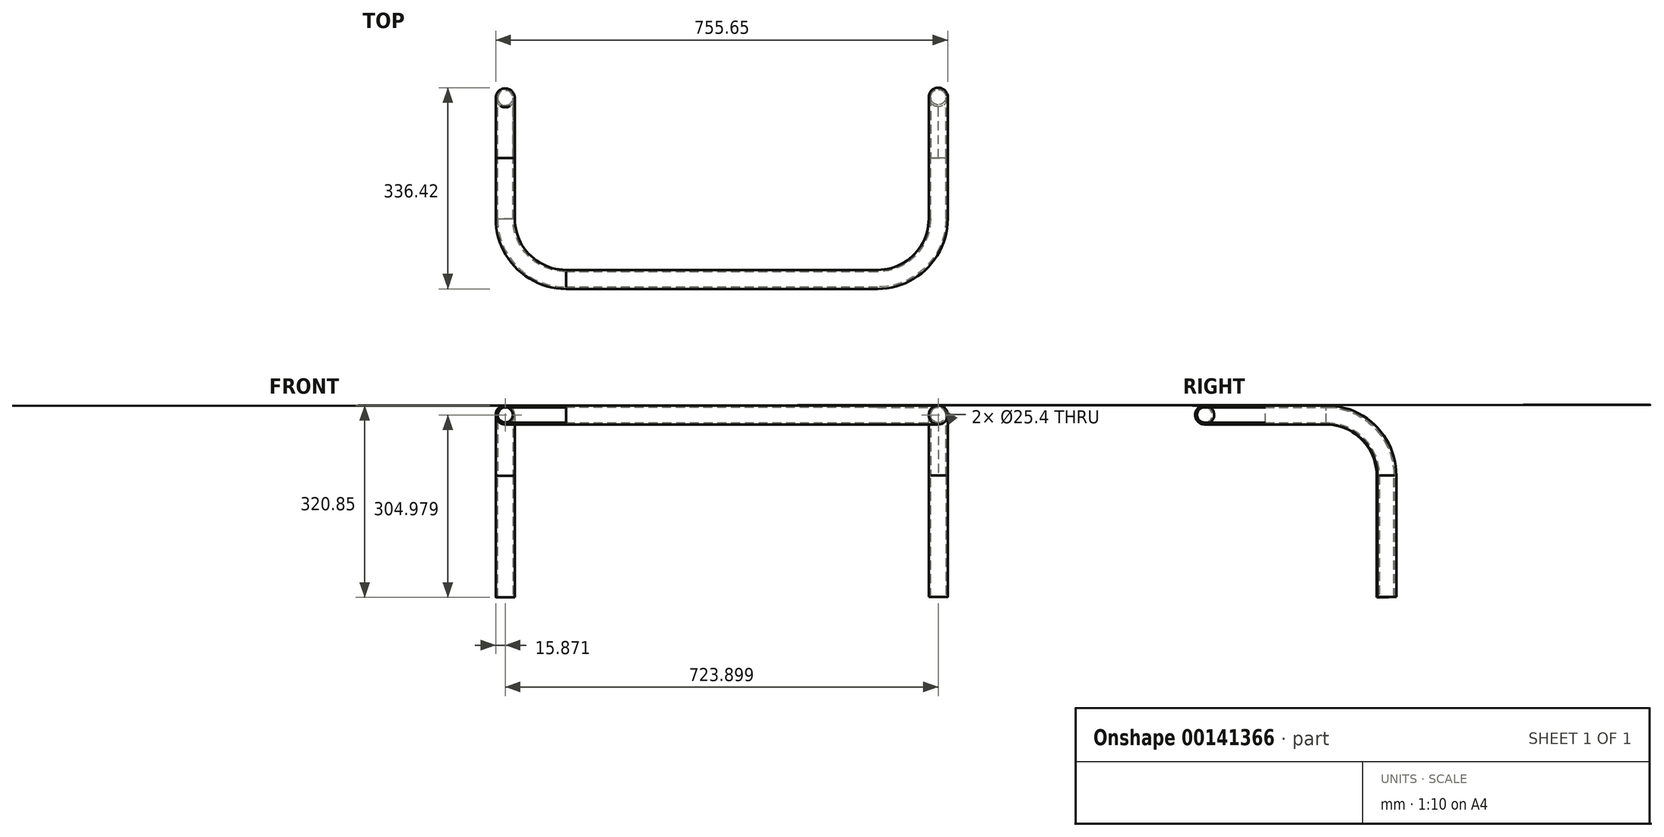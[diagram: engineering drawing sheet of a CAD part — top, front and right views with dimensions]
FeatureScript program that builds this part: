
annotation { "Feature Type Name" : "Feature", "Feature Type Description" : "" }
export const myFeature = defineFeature(function(context is Context, id is Id, definition is map)
    precondition{}
    {
        {
            var Q0;
            Q0=qCreatedBy(makeId("Front.planeOp"),FACE);
            var sketch = newSketch(context, id + "F0", { "sketchPlane" : qUnion([Q0])});
            skLineSegment(sketch, "E0", {"start": v(-57.71, 3.81) * mm, "end": v(-57.71, 207.01) * mm});
            skLineSegment(sketch, "E1", {"start": v(666.19, 207.01) * mm, "end": v(666.19, 3.81) * mm});
            skLineSegment(sketch, "E2", {"start": v(43.89, 308.61) * mm, "end": v(564.59, 308.61) * mm});
            skSolve(sketch);
        }
        {
            var Q0;
            Q0=sQuery(id+"F0.wireOp",EDGE,"mjDuWlF3-Q2C5-AVhh-5H8Y-v2cNqstjDBgE");
            var Q1;
            Q1=sQuery(id+"F0.wireOp",EDGE,"E2");
            cPlane(context, id + "F1", {"entities" : qUnion([Q0, Q1]), "cplaneType" : CPlaneType.LINE_ANGLE, "offset" : 25.4 * mm, "angle" : 90 * degree, "width" : 152.4 * mm, "height" : 152.4 * mm});
        }
        {
            var Q0;
            Q0=qCreatedBy(id+"F1.planeOp",FACE);
            var sketch = newSketch(context, id + "F2", { "sketchPlane" : qUnion([Q0])});
            skLineSegment(sketch, "E3", {"start": v(665.66, -202.81) * mm, "end": v(665.66, -304.41) * mm});
            skLineSegment(sketch, "E4", {"start": v(-58.24, -304.41) * mm, "end": v(-58.24, -202.81) * mm});
            skLineSegment(sketch, "E5", {"start": v(348.15, -304.41) * mm, "end": v(348.15, -202.81) * mm});
            skSolve(sketch);
        }
        {
            var Q0;
            Q0=qCreatedBy(makeId("Top.planeOp"),FACE);
            var sketch = newSketch(context, id + "F3", { "sketchPlane" : qUnion([Q0])});
            skLineSegment(sketch, "E6", {"start": v(-58.24, -304.41) * mm, "end": v(-58.24, -101.21) * mm});
            skCircle(sketch, "E7", {"center": v(-57.71, 0) * mm, "radius": 15.88 * mm});
            skSolve(sketch);
        }
        {
            var Q0;
            Q0=sQuery(id+"F2.wireOp",VERTEX,"E4.start");
            var Q1;
            Q1=sQuery(id+"F2.wireOp",VERTEX,"E5.start");
            var Q2;
            Q2=sQuery(id+"F3.wireOp",VERTEX,"E6.start");
            cPlane(context, id + "F4", {"entities" : qUnion([Q0, Q1, Q2]), "cplaneType" : CPlaneType.THREE_POINT, "offset" : 25.4 * mm, "width" : 152.4 * mm, "height" : 152.4 * mm});
        }
        {
            var Q0;
            Q0=qCreatedBy(id+"F4.planeOp",FACE);
            var sketch = newSketch(context, id + "F5", { "sketchPlane" : qUnion([Q0])});
            skCircle(sketch, "E8", {"center": v(-58.24, 324.49) * mm, "radius": 15.88 * mm});
            skCircle(sketch, "E9.1.0.0", {"center": v(665.66, 324.49) * mm, "radius": 15.88 * mm});
            skLineSegment(sketch, "E9.direction1", {"start": v(-58.24, 324.49) * mm, "end": v(665.66, 324.49) * mm, "construction": true});
            skSolve(sketch);
        }
        {
            var Q0;
            Q0=makeQuery(id+"F5.imprint","IMPRINT",FACE,{"disambiguationData":[TD([[makeQuery(id+"F5.imprint","IMPRINT",EDGE,{"derivedFrom":sQuery(id+"F5.wireOp",EDGE,"E8")}),1.0]])]});
            var Q1;
            Q1=sQuery(id+"F2.wireOp",EDGE,"E4");
            sweep(context, id + "F6", {"profiles" : qUnion([Q0]), "path" : qUnion([Q1])});
        }
        {
            var Q0;
            Q0=qCreatedBy(makeId("Right.planeOp"),FACE);
            var sketch = newSketch(context, id + "F7", { "sketchPlane" : qUnion([Q0])});
            skArc(sketch, "E10", {"start": v(2.2, 217.22) * mm, "mid": v(-27.59, 288.26) * mm, "end": v(-98.67, 317.97) * mm});
            skSolve(sketch);
        }
        {
            var Q0;
            Q0=makeQuery(id+"F6.opSweep","CAP_FACE",FACE,{"disambiguationData":[OSD([sQuery(id+"F2.wireOp",VERTEX,"E4.end"),sQuery(id+"F5.wireOp",EDGE,"E8")])],"isStart":false});
            var sketch = newSketch(context, id + "F8", { "sketchPlane" : qUnion([Q0])});
            skLineSegment(sketch, "E11", {"start": v(58.24, 324.49) * mm, "end": v(-68.76, 324.49) * mm});
            skSolve(sketch);
        }
        {
            var Q0;
            Q0 = qBodyType(qCreatedBy(id + "F8" ,EDGE), BodyType.WIRE);
            cPlane(context, id + "F9", {"entities" : qUnion([Q0]), "cplaneType" : CPlaneType.LINE_ANGLE, "offset" : 25.4 * mm, "angle" : 90 * degree, "width" : 152.4 * mm, "height" : 152.4 * mm});
        }
        {
            var Q0;
            Q0=qCreatedBy(id+"F9.planeOp",FACE);
            var sketch = newSketch(context, id + "F10", { "sketchPlane" : qUnion([Q0])});
            skLineSegment(sketch, "E12", {"start": v(-58.27, -202.8) * mm, "end": v(-58.27, -75.8) * mm});
            skSolve(sketch);
        }
        {
            var Q0;
            Q0=sQuery(id+"F10.wireOp",EDGE,"E12");
            cPlane(context, id + "F11", {"entities" : qUnion([Q0]), "cplaneType" : CPlaneType.LINE_ANGLE, "offset" : 25.4 * mm, "angle" : 90 * degree, "width" : 152.4 * mm, "height" : 152.4 * mm});
        }
        {
            var Q0;
            Q0=qCreatedBy(id+"F11.planeOp",FACE);
            var sketch = newSketch(context, id + "F12", { "sketchPlane" : qUnion([Q0])});
            skLineSegment(sketch, "E13", {"start": v(-102.45, 324.5) * mm, "end": v(-204.05, 324.5) * mm});
            skLineSegment(sketch, "E14", {"start": v(-204.05, 324.5) * mm, "end": v(-204.05, 222.9) * mm});
            skArc(sketch, "E15", {"start": v(-102.45, 222.9) * mm, "mid": v(-132.21, 294.75) * mm, "end": v(-204.05, 324.5) * mm});
            skLineSegment(sketch, "E16", {"start": v(-204.05, 222.9) * mm, "end": v(-102.45, 222.9) * mm});
            skSolve(sketch);
        }
        {
            var Q0;
            Q0=makeQuery(id+"F6.opSweep","CAP_FACE",FACE,{"disambiguationData":[OSD([sQuery(id+"F2.wireOp",VERTEX,"E4.end"),sQuery(id+"F5.wireOp",EDGE,"E8")])],"isStart":false});
            var Q1;
            Q1=makeQuery(id+"F6.opSweep","CAP_FACE",FACE,{"disambiguationData":[OSD([sQuery(id+"F2.wireOp",VERTEX,"E4.end"),sQuery(id+"F5.wireOp",EDGE,"E9.1.0.0")])],"isStart":false});
            var Q2;
            Q2=sQuery(id+"F12.wireOp",EDGE,"E15");
            sweep(context, id + "F13", {"operationType" : NewBodyOperationType.ADD, "profiles" : qUnion([Q0, Q1]), "path" : qUnion([Q2])});
        }
        {
            var Q0;
            Q0=makeQuery(id+"F13.opSweep","CAP_FACE",FACE,{"disambiguationData":[OSD([sQuery(id+"F2.wireOp",VERTEX,"E4.end"),sQuery(id+"F5.wireOp",EDGE,"E8"),sQuery(id+"F7.wireOp",VERTEX,"E10.start")])],"isStart":false});
            var Q1;
            Q1=makeQuery(id+"F13.opSweep","CAP_FACE",FACE,{"disambiguationData":[OSD([sQuery(id+"F2.wireOp",VERTEX,"E4.end"),sQuery(id+"F5.wireOp",EDGE,"E9.1.0.0"),sQuery(id+"F7.wireOp",VERTEX,"E10.start")])],"isStart":false});
            var Q2;
            Q2=sQuery(id+"F0.wireOp",EDGE,"E0");
            sweep(context, id + "F14", {"operationType" : NewBodyOperationType.ADD, "profiles" : qUnion([Q0, Q1]), "path" : qUnion([Q2])});
        }
        {
            var Q0;
            Q0=makeQuery(id+"F6.opSweep","CAP_FACE",FACE,{"disambiguationData":[OSD([sQuery(id+"F2.wireOp",VERTEX,"E4.start"),sQuery(id+"F5.wireOp",EDGE,"E8")])],"isStart":true});
            var sketch = newSketch(context, id + "F15", { "sketchPlane" : qUnion([Q0])});
            skLineSegment(sketch, "E17", {"start": v(-58.24, 324.49) * mm, "end": v(-397.35, 324.49) * mm});
            skSolve(sketch);
        }
        {
            var Q0;
            Q0=sQuery(id+"F15.wireOp",EDGE,"E17");
            cPlane(context, id + "F16", {"entities" : qUnion([Q0]), "cplaneType" : CPlaneType.LINE_ANGLE, "offset" : 25.4 * mm, "angle" : 90 * degree, "width" : 152.4 * mm, "height" : 152.4 * mm});
        }
        {
            var Q0;
            Q0=qCreatedBy(id+"F16.planeOp",FACE);
            var sketch = newSketch(context, id + "F17", { "sketchPlane" : qUnion([Q0])});
            skLineSegment(sketch, "E18", {"start": v(-58.24, -304.42) * mm, "end": v(43.36, -304.42) * mm});
            skLineSegment(sketch, "E19", {"start": v(43.36, -304.42) * mm, "end": v(43.36, -406.02) * mm});
            skArc(sketch, "E20", {"start": v(-58.24, -304.42) * mm, "mid": v(-28.48, -376.26) * mm, "end": v(43.36, -406.02) * mm});
            skLineSegment(sketch, "E21", {"start": v(43.36, -304.42) * mm, "end": v(564.06, -304.42) * mm});
            skLineSegment(sketch, "E22", {"start": v(564.06, -304.42) * mm, "end": v(564.06, -406.02) * mm});
            skLineSegment(sketch, "E23", {"start": v(564.06, -304.42) * mm, "end": v(665.66, -304.42) * mm});
            skArc(sketch, "E24", {"start": v(564.06, -406.02) * mm, "mid": v(635.9, -376.26) * mm, "end": v(665.66, -304.42) * mm});
            skSolve(sketch);
        }
        {
            var Q0;
            Q0=makeQuery(id+"F15.imprint","IMPRINT",FACE,{"disambiguationData":[TD([[makeQuery(id+"F15.imprint","IMPRINT",EDGE,{"derivedFrom":makeQuery(id+"F6.opSweep","CAP_EDGE",EDGE,{"disambiguationData":[OSD([sQuery(id+"F2.wireOp",VERTEX,"E4.start"),sQuery(id+"F5.wireOp",EDGE,"E8")])],"isStart":true})}),-1.0]])]});
            var Q1;
            Q1=sQuery(id+"F17.wireOp",EDGE,"E20");
            sweep(context, id + "F18", {"operationType" : NewBodyOperationType.ADD, "profiles" : qUnion([Q0]), "path" : qUnion([Q1])});
        }
        {
            var Q0;
            Q0=makeQuery(id+"F18.opSweep","CAP_FACE",FACE,{"disambiguationData":[OSD([sQuery(id+"F2.wireOp",VERTEX,"E4.start"),sQuery(id+"F5.wireOp",EDGE,"E8"),sQuery(id+"F17.wireOp",VERTEX,"E20.end")])],"isStart":false});
            var Q1;
            Q1=sQuery(id+"F0.wireOp",EDGE,"E2");
            sweep(context, id + "F19", {"operationType" : NewBodyOperationType.ADD, "profiles" : qUnion([Q0]), "path" : qUnion([Q1])});
        }
        {
            var Q0;
            Q0=makeQuery(id+"F19.opSweep","CAP_FACE",FACE,{"disambiguationData":[OSD([sQuery(id+"F0.wireOp",VERTEX,"E2.end"),sQuery(id+"F2.wireOp",VERTEX,"E4.start"),sQuery(id+"F5.wireOp",EDGE,"E8"),sQuery(id+"F17.wireOp",VERTEX,"E20.end")])],"isStart":false});
            var Q1;
            Q1=sQuery(id+"F17.wireOp",EDGE,"E24");
            sweep(context, id + "F20", {"operationType" : NewBodyOperationType.ADD, "profiles" : qUnion([Q0]), "path" : qUnion([Q1])});
        }
        {
            var Q0;
            Q0=makeQuery(id+"F20.opSweep","CAP_FACE",FACE,{"disambiguationData":[OSD([sQuery(id+"F0.wireOp",VERTEX,"E2.end"),sQuery(id+"F2.wireOp",VERTEX,"E4.start"),sQuery(id+"F5.wireOp",EDGE,"E8"),sQuery(id+"F17.wireOp",VERTEX,"E20.end"),sQuery(id+"F17.wireOp",VERTEX,"E24.end")])],"isStart":false});
            var Q1;
            Q1=sQuery(id+"F2.wireOp",EDGE,"E3");
            sweep(context, id + "F21", {"operationType" : NewBodyOperationType.ADD, "profiles" : qUnion([Q0]), "path" : qUnion([Q1])});
        }
        {
            var Q0;
            Q0=makeQuery(id+"F21.opSweep","CAP_FACE",FACE,{"disambiguationData":[OSD([sQuery(id+"F0.wireOp",VERTEX,"E2.end"),sQuery(id+"F2.wireOp",VERTEX,"E3.start"),sQuery(id+"F2.wireOp",VERTEX,"E4.start"),sQuery(id+"F5.wireOp",EDGE,"E8"),sQuery(id+"F17.wireOp",VERTEX,"E20.end"),sQuery(id+"F17.wireOp",VERTEX,"E24.end")])],"isStart":false});
            var sketch = newSketch(context, id + "F22", { "sketchPlane" : qUnion([Q0])});
            skLineSegment(sketch, "E25", {"start": v(-665.66, 324.49) * mm, "end": v(-767.26, 324.49) * mm});
            skSolve(sketch);
        }
        {
            var Q0;
            Q0=sQuery(id+"F22.wireOp",EDGE,"E25");
            cPlane(context, id + "F23", {"entities" : qUnion([Q0]), "cplaneType" : CPlaneType.LINE_ANGLE, "offset" : 25.4 * mm, "angle" : 90 * degree, "width" : 152.4 * mm, "height" : 152.4 * mm});
        }
        {
            var Q0;
            Q0=qCreatedBy(id+"F23.planeOp",FACE);
            var sketch = newSketch(context, id + "F24", { "sketchPlane" : qUnion([Q0])});
            skLineSegment(sketch, "E26", {"start": v(665.73, -202.84) * mm, "end": v(665.73, -101.24) * mm});
            skSolve(sketch);
        }
        {
            var Q0;
            Q0=sQuery(id+"F24.wireOp",EDGE,"E26");
            cPlane(context, id + "F25", {"entities" : qUnion([Q0]), "cplaneType" : CPlaneType.LINE_ANGLE, "offset" : 25.4 * mm, "angle" : 270 * degree, "width" : 152.4 * mm, "height" : 152.4 * mm});
        }
        {
            var Q0;
            Q0=qCreatedBy(id+"F25.planeOp",FACE);
            var sketch = newSketch(context, id + "F26", { "sketchPlane" : qUnion([Q0])});
            skLineSegment(sketch, "E27", {"start": v(202.8, 324.62) * mm, "end": v(101.2, 324.62) * mm});
            skLineSegment(sketch, "E28", {"start": v(202.8, 324.62) * mm, "end": v(202.8, 223.02) * mm});
            skArc(sketch, "E29", {"start": v(202.8, 324.62) * mm, "mid": v(130.96, 294.87) * mm, "end": v(101.2, 223.02) * mm});
            skLineSegment(sketch, "E30", {"start": v(202.8, 223.02) * mm, "end": v(101.2, 223.02) * mm});
            skSolve(sketch);
        }
        {
            var Q0;
            Q0=makeQuery(id+"F21.opSweep","CAP_FACE",FACE,{"disambiguationData":[OSD([sQuery(id+"F0.wireOp",VERTEX,"E2.end"),sQuery(id+"F2.wireOp",VERTEX,"E3.start"),sQuery(id+"F2.wireOp",VERTEX,"E4.start"),sQuery(id+"F5.wireOp",EDGE,"E8"),sQuery(id+"F17.wireOp",VERTEX,"E20.end"),sQuery(id+"F17.wireOp",VERTEX,"E24.end")])],"isStart":false});
            var Q1;
            Q1=sQuery(id+"F26.wireOp",EDGE,"E29");
            sweep(context, id + "F27", {"operationType" : NewBodyOperationType.ADD, "profiles" : qUnion([Q0]), "path" : qUnion([Q1])});
        }
        {
            var Q0;
            Q0=makeQuery(id+"F27.opSweep","CAP_FACE",FACE,{"disambiguationData":[OSD([sQuery(id+"F0.wireOp",VERTEX,"E2.end"),sQuery(id+"F2.wireOp",VERTEX,"E4.start"),sQuery(id+"F3.wireOp",VERTEX,"E6.end"),sQuery(id+"F5.wireOp",EDGE,"E8"),sQuery(id+"F7.wireOp",VERTEX,"E10.start"),sQuery(id+"F17.wireOp",VERTEX,"E20.end"),sQuery(id+"F17.wireOp",VERTEX,"E24.end")])],"isStart":false});
            var Q1;
            Q1=sQuery(id+"F0.wireOp",EDGE,"E1");
            sweep(context, id + "F28", {"operationType" : NewBodyOperationType.ADD, "profiles" : qUnion([Q0]), "path" : qUnion([Q1])});
        }
        {
            var Q0;
            Q0=makeQuery(id+"F14.opSweep","CAP_FACE",FACE,{"disambiguationData":[OSD([sQuery(id+"F0.wireOp",VERTEX,"E0.start"),sQuery(id+"F2.wireOp",VERTEX,"E4.end"),sQuery(id+"F5.wireOp",EDGE,"E8"),sQuery(id+"F7.wireOp",VERTEX,"E10.start")])],"isStart":false});
            var Q1;
            Q1=makeQuery(id+"F28.opSweep","CAP_FACE",FACE,{"disambiguationData":[OSD([sQuery(id+"F0.wireOp",VERTEX,"E1.end"),sQuery(id+"F0.wireOp",VERTEX,"E2.end"),sQuery(id+"F2.wireOp",VERTEX,"E4.start"),sQuery(id+"F3.wireOp",VERTEX,"E6.end"),sQuery(id+"F5.wireOp",EDGE,"E8"),sQuery(id+"F7.wireOp",VERTEX,"E10.start"),sQuery(id+"F17.wireOp",VERTEX,"E20.end"),sQuery(id+"F17.wireOp",VERTEX,"E24.end")])],"isStart":false});
            shell(context, id + "F29", {"entities" : qUnion([Q0, Q1]), "thickness" : 3.17 * mm});
        }
    });
